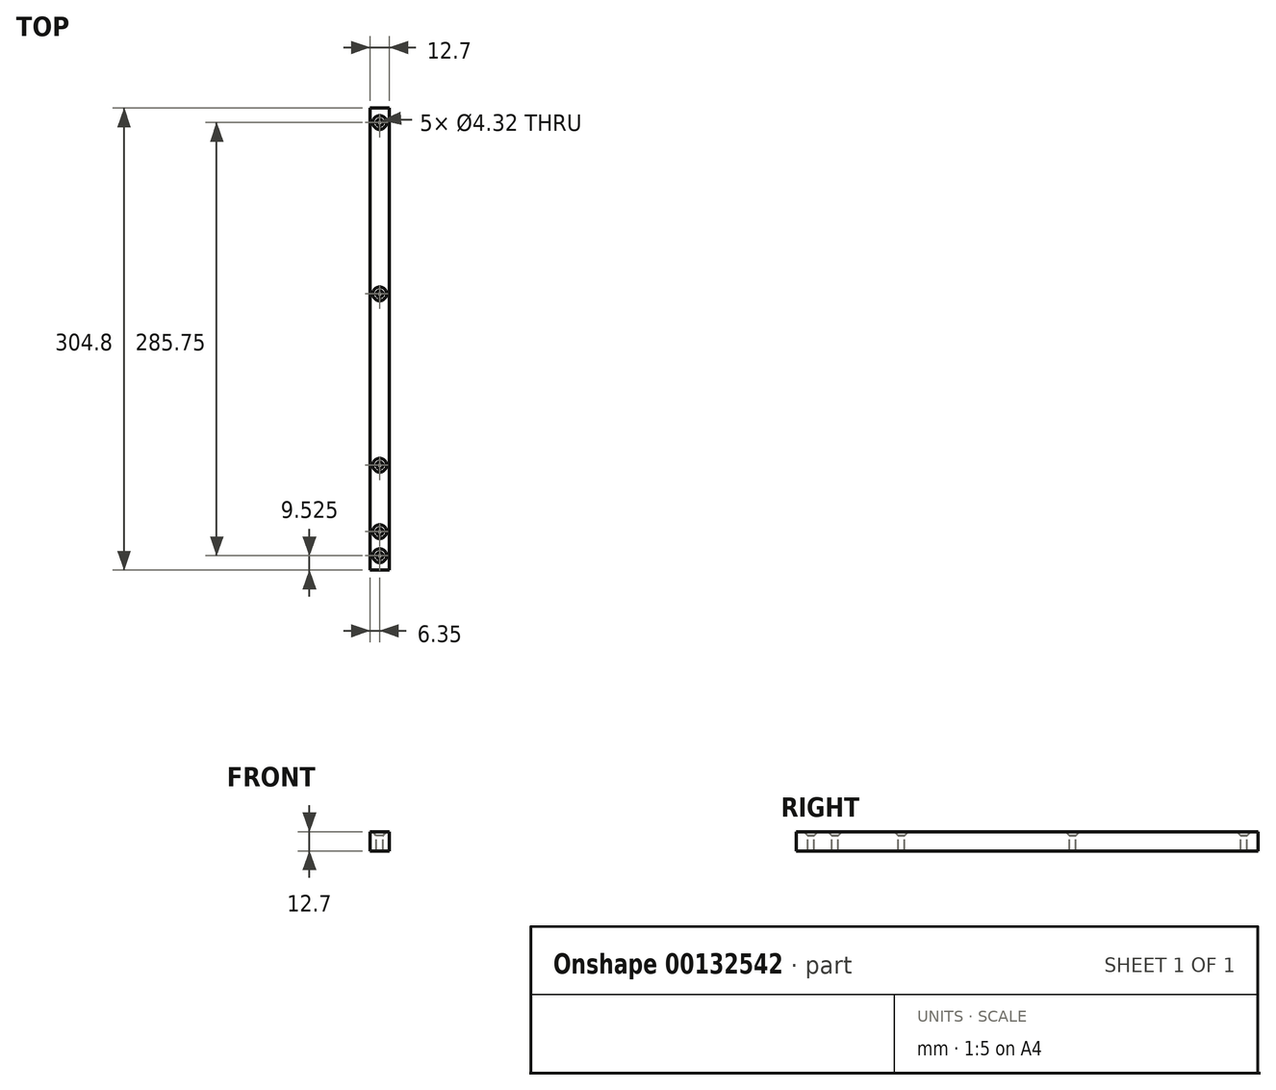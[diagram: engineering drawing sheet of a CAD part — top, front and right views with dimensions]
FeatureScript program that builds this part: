
annotation { "Feature Type Name" : "Feature", "Feature Type Description" : "" }
export const myFeature = defineFeature(function(context is Context, id is Id, definition is map)
    precondition{}
    {
        {
            var Q0;
            Q0=qCreatedBy(makeId("Front.planeOp"),FACE);
            var sketch = newSketch(context, id + "F0", { "sketchPlane" : qUnion([Q0])});
            skLineSegment(sketch, "E0.bottom", {"start": v(0, 0) * mm, "end": v(12.7, 0) * mm});
            skLineSegment(sketch, "E0.top", {"start": v(0, 12.7) * mm, "end": v(12.7, 12.7) * mm});
            skLineSegment(sketch, "E0.left", {"start": v(0, 0) * mm, "end": v(0, 12.7) * mm});
            skLineSegment(sketch, "E0.right", {"start": v(12.7, 0) * mm, "end": v(12.7, 12.7) * mm});
            skSolve(sketch);
        }
        {
            var Q0;
            Q0=makeQuery(id+"F0.imprint","IMPRINT",FACE,{"disambiguationData":[TD([[makeQuery(id+"F0.imprint","IMPRINT",EDGE,{"derivedFrom":sQuery(id+"F0.wireOp",EDGE,"E0.bottom")}),1.0]])]});
            extrude(context, id + "F1", {"entities" : qUnion([Q0]), "depth" : 304.8 * mm});
        }
        {
            var Q0;
            Q0=makeQuery(id+"F1.opExtrude","SWEPT_FACE",FACE,{"disambiguationData":[OSD([sQuery(id+"F0.wireOp",EDGE,"E0.top")])]});
            var sketch = newSketch(context, id + "F2", { "sketchPlane" : qUnion([Q0])});
            skPoint(sketch, "E1", {"position": v(6.35, -9.53) * mm});
            skPoint(sketch, "E1.positionSnap0", {"position": v(6.35, 0) * mm});
            skPoint(sketch, "E2", {"position": v(6.35, -122.56) * mm});
            skPoint(sketch, "E3", {"position": v(6.35, -235.59) * mm});
            skPoint(sketch, "E4", {"position": v(6.35, -295.28) * mm});
            skPoint(sketch, "E4.positionSnap0", {"position": v(6.35, -304.8) * mm});
            skPoint(sketch, "E5", {"position": v(6.35, -279.4) * mm});
            skSolve(sketch);
        }
        {
            var Q0;
            Q0=sQuery(id+"F2.wireOp",VERTEX,"E1");
            var Q1;
            Q1=sQuery(id+"F2.wireOp",VERTEX,"E2");
            var Q2;
            Q2=sQuery(id+"F2.wireOp",VERTEX,"E3");
            var Q3;
            Q3=sQuery(id+"F2.wireOp",VERTEX,"E5");
            var Q4;
            Q4=sQuery(id+"F2.wireOp",VERTEX,"E4");
            var Q5;
            Q5=makeQuery(id+"F1.opExtrude","SWEPT_BODY",BODY,{"disambiguationData":[OSD([sQuery(id+"F0.wireOp",EDGE,"E0.bottom"),sQuery(id+"F0.wireOp",EDGE,"E0.top"),sQuery(id+"F0.wireOp",EDGE,"E0.left"),sQuery(id+"F0.wireOp",EDGE,"E0.right")])]});
            hole(context, id + "F3", {"style" : HoleStyle.C_SINK, "endStyle" : HoleEndStyle.THROUGH, "standardTappedOrClearance" : lookupTablePath({ "standard" : "ANSI", "fit" : "Close", "size" : "#8", "type" : "Clearance" }), "standardBlindInLast" : lookupTablePath({ "fit" : "Close", "standard" : "ANSI", "size" : "#8", "type" : "Clearance" }), "holeDiameter" : 4.32 * mm, "cSinkDiameter" : 9.12 * mm, "cSinkAngle" : 82 * degree, "locations" : qUnion([Q0, Q1, Q2, Q3, Q4]), "scope" : qUnion([Q5]), "isTappedThrough" : true});
        }
    });
